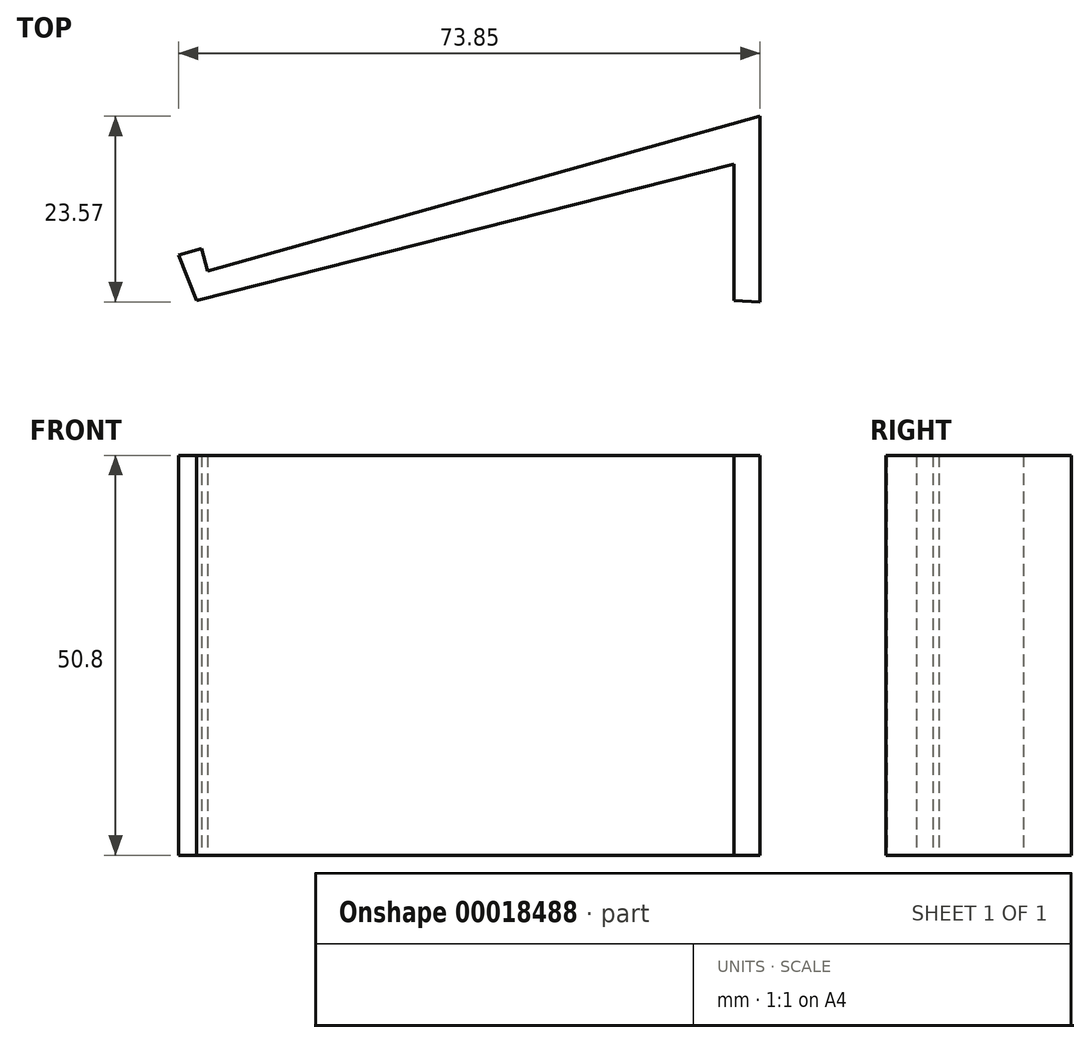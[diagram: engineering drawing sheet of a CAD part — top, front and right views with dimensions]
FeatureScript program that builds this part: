
annotation { "Feature Type Name" : "Feature", "Feature Type Description" : "" }
export const myFeature = defineFeature(function(context is Context, id is Id, definition is map)
    precondition{}
    {
        {
            var Q0;
            Q0=qCreatedBy(makeId("Top.planeOp"),FACE);
            var sketch = newSketch(context, id + "F0", { "sketchPlane" : qUnion([Q0])});
            skLineSegment(sketch, "E0", {"start": v(-41.32, 0) * mm, "end": v(26.9, 17.33) * mm});
            skLineSegment(sketch, "E1", {"start": v(26.9, 17.33) * mm, "end": v(26.9, 0) * mm});
            skLineSegment(sketch, "E2", {"start": v(26.9, 0) * mm, "end": v(30.23, -0.14) * mm});
            skLineSegment(sketch, "E3", {"start": v(30.23, -0.14) * mm, "end": v(30.23, 23.43) * mm});
            skLineSegment(sketch, "E4", {"start": v(30.23, 23.43) * mm, "end": v(-39.94, 3.74) * mm});
            skLineSegment(sketch, "E5", {"start": v(-39.94, 3.74) * mm, "end": v(-40.74, 6.61) * mm});
            skLineSegment(sketch, "E6", {"start": v(-40.74, 6.61) * mm, "end": v(-43.62, 5.8) * mm});
            skLineSegment(sketch, "E7", {"start": v(-43.62, 5.8) * mm, "end": v(-41.32, 0) * mm});
            skSolve(sketch);
        }
        {
            var Q0;
            Q0 = qSketchRegion(id + "F0", true);
            extrude(context, id + "F1", {"entities" : qUnion([Q0]), "depth" : 25.4 * mm});
        }
        {
            var Q0;
            Q0=makeQuery(id+"F1.opExtrude","CAP_FACE",FACE,{"disambiguationData":[OSD([sQuery(id+"F0.wireOp",EDGE,"E0"),sQuery(id+"F0.wireOp",EDGE,"E1"),sQuery(id+"F0.wireOp",EDGE,"E2"),sQuery(id+"F0.wireOp",EDGE,"E3"),sQuery(id+"F0.wireOp",EDGE,"E4"),sQuery(id+"F0.wireOp",EDGE,"E5"),sQuery(id+"F0.wireOp",EDGE,"E6"),sQuery(id+"F0.wireOp",EDGE,"E7")])],"isStart":false});
            extrude(context, id + "F2", {"entities" : qUnion([Q0]), "operationType" : NewBodyOperationType.ADD, "depth" : 25.4 * mm});
        }
    });
